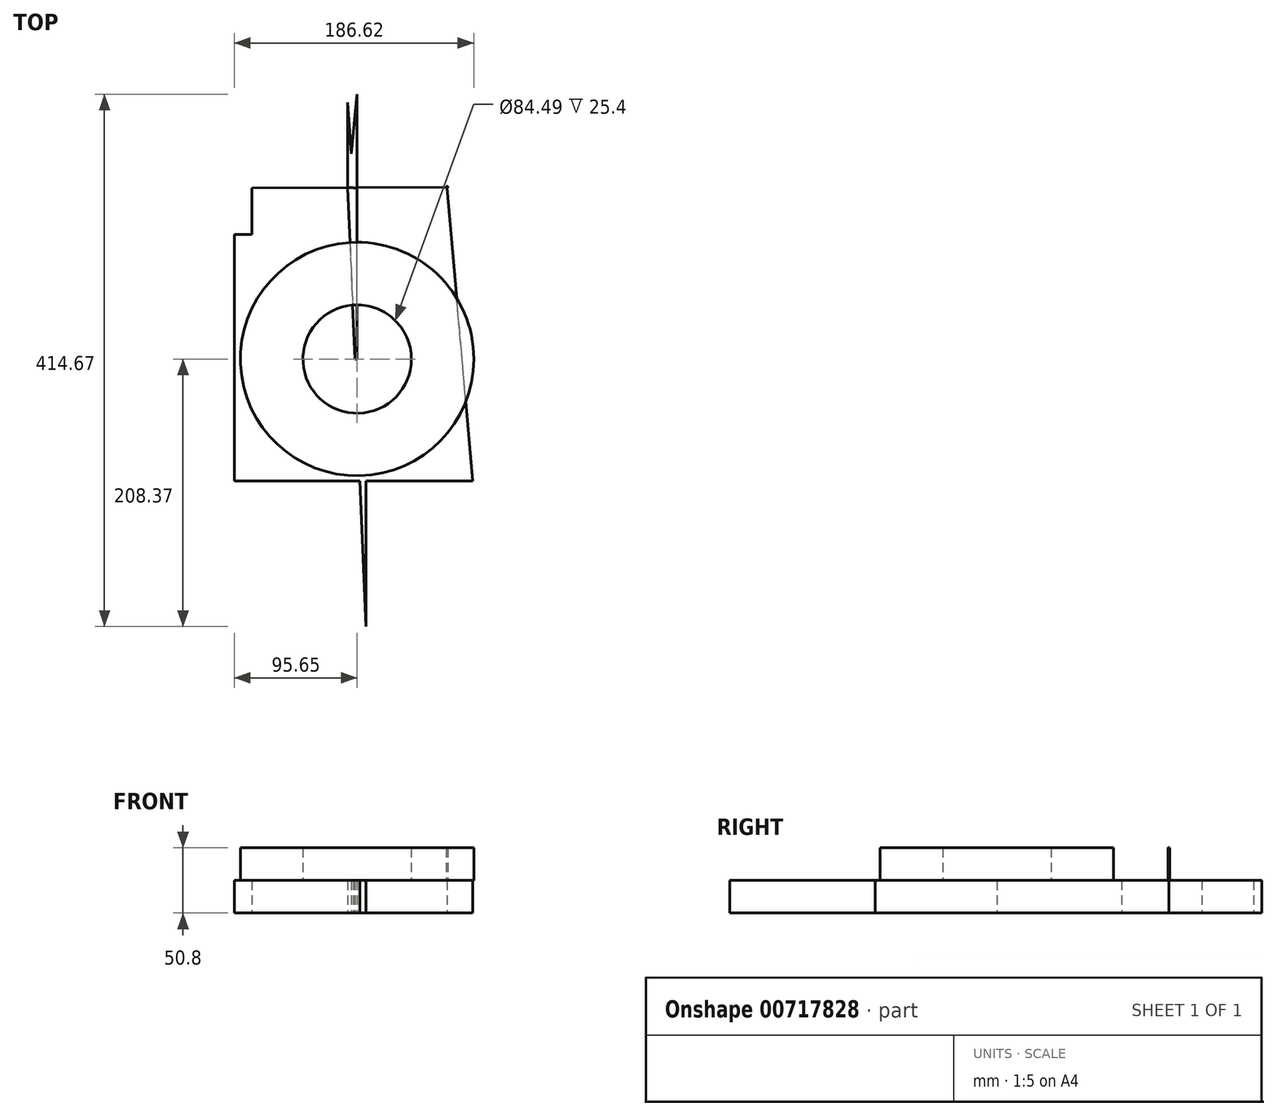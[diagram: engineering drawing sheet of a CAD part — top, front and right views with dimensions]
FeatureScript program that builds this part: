
annotation { "Feature Type Name" : "Feature", "Feature Type Description" : "" }
export const myFeature = defineFeature(function(context is Context, id is Id, definition is map)
    precondition{}
    {
        {
            var Q0;
            Q0=qCreatedBy(makeId("Top.planeOp"),FACE);
            var sketch = newSketch(context, id + "F0", { "sketchPlane" : qUnion([Q0])});
            skLineSegment(sketch, "E0.bottom", {"start": v(0, 0) * mm, "end": v(-95.65, 0) * mm});
            skLineSegment(sketch, "E0.top", {"start": v(0, 97.1) * mm, "end": v(-95.65, 97.1) * mm});
            skLineSegment(sketch, "E0.left", {"start": v(0, 0) * mm, "end": v(0, 97.1) * mm});
            skLineSegment(sketch, "E0.right", {"start": v(-95.65, 0) * mm, "end": v(-95.65, 97.1) * mm});
            skLineSegment(sketch, "E1.bottom", {"start": v(-82.17, 97.1) * mm, "end": v(0, 97.1) * mm});
            skLineSegment(sketch, "E1.top", {"start": v(-82.17, 133.26) * mm, "end": v(0, 133.26) * mm});
            skLineSegment(sketch, "E1.left", {"start": v(-82.17, 97.1) * mm, "end": v(-82.17, 133.26) * mm});
            skLineSegment(sketch, "E1.right", {"start": v(0, 97.1) * mm, "end": v(0, 133.26) * mm});
            skLineSegment(sketch, "E2", {"start": v(0, 133.26) * mm, "end": v(0, 206.3) * mm});
            skLineSegment(sketch, "E3", {"start": v(0, 206.3) * mm, "end": v(-7.37, 133.26) * mm});
            skLineSegment(sketch, "E4", {"start": v(-7.37, 133.26) * mm, "end": v(6.88, -208.37) * mm});
            skLineSegment(sketch, "E5", {"start": v(6.88, -208.37) * mm, "end": v(6.88, -13.35) * mm});
            skLineSegment(sketch, "E6", {"start": v(6.88, -13.35) * mm, "end": v(-7.37, 200.1) * mm});
            skLineSegment(sketch, "E7", {"start": v(-7.37, 200.1) * mm, "end": v(-7.37, 133.26) * mm});
            skLineSegment(sketch, "E8", {"start": v(-95.65, 0) * mm, "end": v(-95.65, -95.03) * mm});
            skLineSegment(sketch, "E9", {"start": v(-95.65, -95.03) * mm, "end": v(2.15, -95.03) * mm});
            skLineSegment(sketch, "E10", {"start": v(2.15, -95.03) * mm, "end": v(90.13, -95.03) * mm});
            skLineSegment(sketch, "E11", {"start": v(90.13, -95.03) * mm, "end": v(70.08, 133.95) * mm});
            skLineSegment(sketch, "E12", {"start": v(70.08, 133.95) * mm, "end": v(-82.17, 133.26) * mm});
            skSolve(sketch);
        }
        {
            var Q0;
            Q0 = qSketchRegion(id + "F0", true);
            extrude(context, id + "F1", {"entities" : qUnion([Q0]), "depth" : 25.4 * mm, "offsetDistance" : 25.4 * mm});
        }
        {
            var Q0;
            Q0=makeQuery(id+"F1.opExtrude","CAP_FACE",FACE,{"disambiguationData":[OSD([sQuery(id+"F0.wireOp",EDGE,"E0.bottom"),sQuery(id+"F0.wireOp",EDGE,"E0.top"),sQuery(id+"F0.wireOp",EDGE,"E0.left"),sQuery(id+"F0.wireOp",EDGE,"E0.right"),sQuery(id+"F0.wireOp",EDGE,"E1.top"),sQuery(id+"F0.wireOp",EDGE,"E1.left"),sQuery(id+"F0.wireOp",EDGE,"E1.right"),sQuery(id+"F0.wireOp",EDGE,"E2"),sQuery(id+"F0.wireOp",EDGE,"E3"),sQuery(id+"F0.wireOp",EDGE,"E4"),sQuery(id+"F0.wireOp",EDGE,"E5"),sQuery(id+"F0.wireOp",EDGE,"E6"),sQuery(id+"F0.wireOp",EDGE,"E7"),sQuery(id+"F0.wireOp",EDGE,"E8"),sQuery(id+"F0.wireOp",EDGE,"E9"),sQuery(id+"F0.wireOp",EDGE,"E10"),sQuery(id+"F0.wireOp",EDGE,"E11"),sQuery(id+"F0.wireOp",EDGE,"E12")])],"isStart":false});
            var sketch = newSketch(context, id + "F2", { "sketchPlane" : qUnion([Q0])});
            skCircle(sketch, "E13", {"center": v(0, 0) * mm, "radius": 42.25 * mm});
            skCircle(sketch, "E14", {"center": v(70.08, 133.95) * mm, "radius": 0.69 * mm});
            skCircle(sketch, "E15", {"center": v(0, 0) * mm, "radius": 90.97 * mm});
            skSolve(sketch);
        }
        {
            var Q0;
            Q0 = qSketchRegion(id + "F2", true);
            extrude(context, id + "F3", {"entities" : qUnion([Q0]), "operationType" : NewBodyOperationType.ADD, "depth" : 25.4 * mm, "offsetDistance" : 25.4 * mm});
        }
    });
